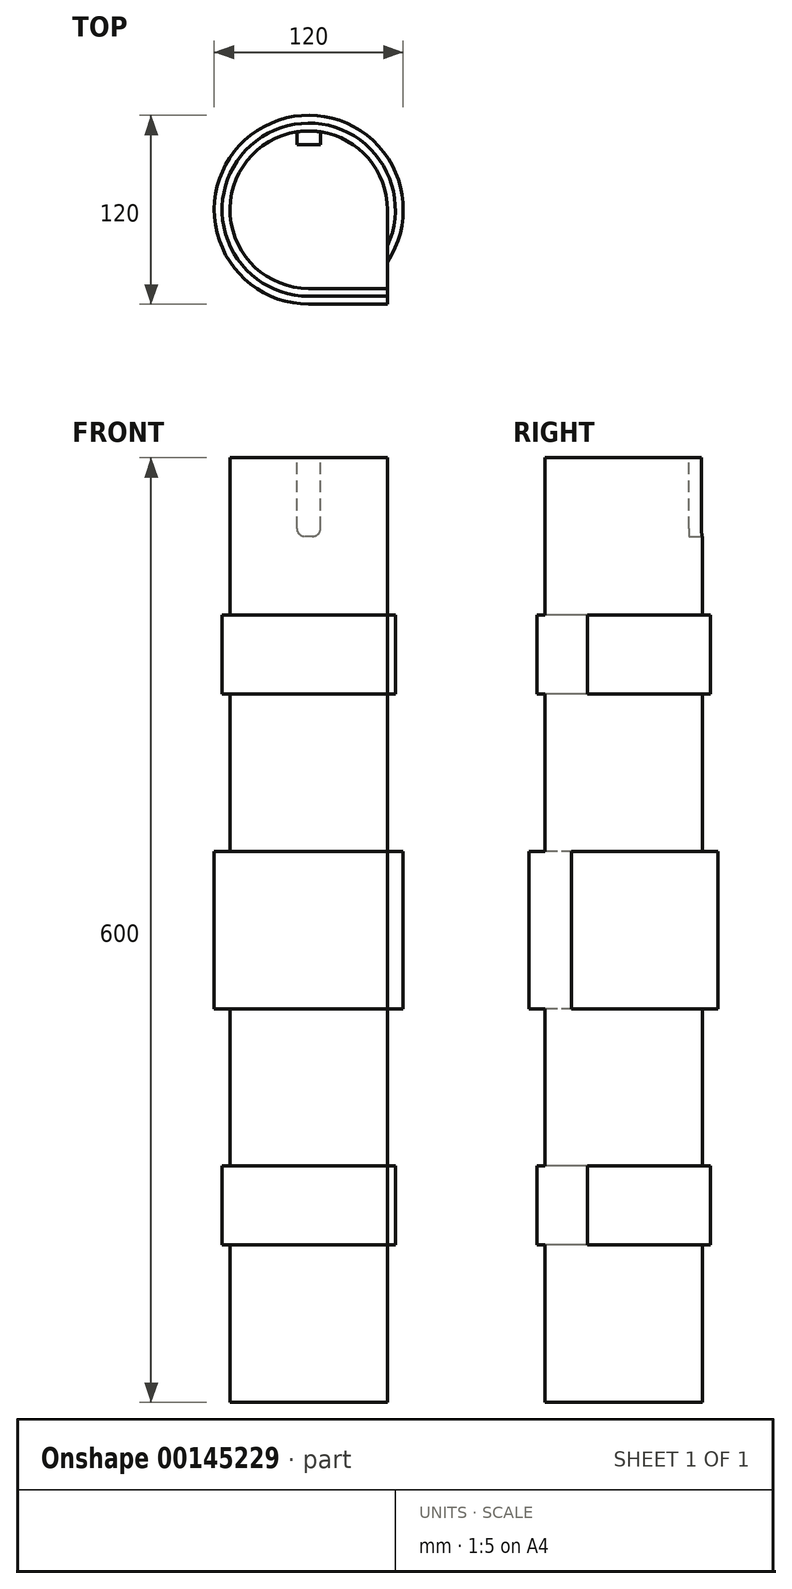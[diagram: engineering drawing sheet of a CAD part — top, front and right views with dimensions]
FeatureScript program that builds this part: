
annotation { "Feature Type Name" : "Feature", "Feature Type Description" : "" }
export const myFeature = defineFeature(function(context is Context, id is Id, definition is map)
    precondition{}
    {
        {
            var Q0;
            Q0=qCreatedBy(makeId("Right.planeOp"),FACE);
            var sketch = newSketch(context, id + "F0", { "sketchPlane" : qUnion([Q0])});
            skLineSegment(sketch, "E0", {"start": v(0, 239.47) * mm, "end": v(0, -360.53) * mm, "construction": true});
            skLineSegment(sketch, "E1", {"start": v(0, -360.53) * mm, "end": v(-50, -360.53) * mm});
            skLineSegment(sketch, "E2", {"start": v(-50, -360.53) * mm, "end": v(-50, -260.53) * mm});
            skLineSegment(sketch, "E3", {"start": v(-50, -260.53) * mm, "end": v(-55, -260.53) * mm});
            skLineSegment(sketch, "E4", {"start": v(-55, -260.53) * mm, "end": v(-55, -210.53) * mm});
            skLineSegment(sketch, "E5", {"start": v(-55, -210.53) * mm, "end": v(-50, -210.53) * mm});
            skLineSegment(sketch, "E6", {"start": v(-50, -210.53) * mm, "end": v(-50, -110.53) * mm});
            skLineSegment(sketch, "E7", {"start": v(-50, -110.53) * mm, "end": v(-60, -110.53) * mm});
            skLineSegment(sketch, "E8", {"start": v(-60, -110.53) * mm, "end": v(-60, -10.53) * mm});
            skLineSegment(sketch, "E9", {"start": v(-60, -10.53) * mm, "end": v(-50, -10.53) * mm});
            skLineSegment(sketch, "E10", {"start": v(-50, -10.53) * mm, "end": v(-50, 89.47) * mm});
            skLineSegment(sketch, "E11", {"start": v(-50, 89.47) * mm, "end": v(-55, 89.47) * mm});
            skLineSegment(sketch, "E12", {"start": v(-55, 89.47) * mm, "end": v(-55, 139.47) * mm});
            skLineSegment(sketch, "E13", {"start": v(-55, 139.47) * mm, "end": v(-50, 139.47) * mm});
            skLineSegment(sketch, "E14", {"start": v(-50, 139.47) * mm, "end": v(-50, 239.47) * mm});
            skLineSegment(sketch, "E15", {"start": v(-50, 239.47) * mm, "end": v(0, 239.47) * mm});
            skLineSegment(sketch, "E16", {"start": v(0, 239.47) * mm, "end": v(0, -360.53) * mm});
            skSolve(sketch);
        }
        {
            var Q0;
            Q0 = qSketchRegion(id + "F0", true);
            var Q1;
            Q1=sQuery(id+"F0.wireOp",EDGE,"E16");
            revolve(context, id + "F1", {"entities" : qUnion([Q0]), "axis" : qUnion([Q1]), "revolveType" : RevolveType.FULL});
        }
        {
            var Q0;
            Q0=makeQuery(id+"F1.opRevolve","SWEPT_FACE",FACE,{"disambiguationData":[OSD([sQuery(id+"F0.wireOp",EDGE,"E15")])]});
            var sketch = newSketch(context, id + "F2", { "sketchPlane" : qUnion([Q0])});
            skLineSegment(sketch, "E17", {"start": v(0, -28.22) * mm, "end": v(0, 77.35) * mm, "construction": true});
            skArc(sketch, "E18.0", {"start": v(7.5, 49.43) * mm, "mid": v(0, 50) * mm, "end": v(-7.5, 49.43) * mm});
            skLineSegment(sketch, "E19.bottom", {"start": v(7.5, 41.43) * mm, "end": v(-7.5, 41.43) * mm});
            skLineSegment(sketch, "E19.left", {"start": v(7.5, 41.43) * mm, "end": v(7.5, 49.43) * mm});
            skLineSegment(sketch, "E19.right", {"start": v(-7.5, 41.43) * mm, "end": v(-7.5, 49.43) * mm});
            skPoint(sketch, "E19.middle", {"position": v(0, 50) * mm});
            skSolve(sketch);
        }
        {
            var Q0;
            Q0 = qSketchRegion(id + "F2", true);
            extrude(context, id + "F3", {"entities" : qUnion([Q0]), "operationType" : NewBodyOperationType.REMOVE, "oppositeDirection" : true, "depth" : 50 * mm});
        }
        {
            var Q0;
            Q0=makeQuery(id+"F3.boolean.opBoolean","COPY",EDGE,{"derivedFrom":makeQuery(id+"F3.opExtrude","CAP_EDGE",EDGE,{"disambiguationData":[OSD([sQuery(id+"F2.wireOp",EDGE,"E19.right")])],"isStart":false})});
            var Q1;
            Q1=makeQuery(id+"F3.boolean.opBoolean","COPY",EDGE,{"derivedFrom":makeQuery(id+"F3.opExtrude","CAP_EDGE",EDGE,{"disambiguationData":[OSD([sQuery(id+"F2.wireOp",EDGE,"E19.left")])],"isStart":false})});
            fillet(context, id + "F4", {"entities" : qUnion([Q0, Q1]), "radius" : 5 * mm, "tangentPropagation" : true, "allowEdgeOverflow" : false});
        }
        {
            var Q0;
            Q0 = qSketchRegion(id + "F0", true);
            extrude(context, id + "F5", {"entities" : qUnion([Q0]), "operationType" : NewBodyOperationType.ADD, "depth" : 50 * mm});
        }
    });
